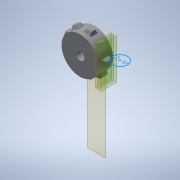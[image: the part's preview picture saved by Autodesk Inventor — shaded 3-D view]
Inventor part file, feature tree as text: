
AUTODESK INVENTOR PART (.ipt)
format: ipt  version: 2020 (Build 240168000, 168)  size: 642,048 bytes
history: native  units: mm
features: other x14, sketch x9, extrude x8, projected_geometry x2, loft x1, pattern_circular x1, chamfer x1, reference x1
ambient origin geometry x8: Origin, YZ Plane, XZ Plane, XY Plane, X Axis, Y Axis, Z Axis, Center Point
bodies: Body1 (feature_tree)
feature tree (37):
  other  "Bryła1"
  other  "Płaszczyzna konstrukcyjna1"
  extrude  "Wyciągnięcie proste1"  Depth=20.0mm
  other  "Płaszczyzna konstrukcyjna2"
  extrude  "Wyciągnięcie proste2"  Depth=50.0mm
  extrude  "Wyciągnięcie proste3"  Depth=20.0mm TaperAngle=0.0deg
  other  "Płaszczyzna konstrukcyjna4"
  other  "Płaszczyzna konstrukcyjna5"
  sketch  "Szkic5"
  other  "Płaszczyzna konstrukcyjna6"
  loft  "Wyciągnięcie złożone1"
  pattern_circular  "Szyk kołowy1"  [2 undecoded]
  extrude  "Wyciągnięcie proste5"  TaperAngle=0.0deg  [1 undecoded]
  other  "Zęby przekładni walcowej1"
  extrude  "Wyciągnięcie proste6"  Depth=3.0mm
  sketch  "Szkic10"
  extrude  "Wyciągnięcie proste9"  Depth=12.0mm
  extrude  "Wyciągnięcie proste8"  Depth=12.0mm
  extrude  "Wyciągnięcie proste10"  [1 undecoded]
  chamfer  "Faza2"  Distance=3.0mm
  sketch  "Szkic1"
  reference  "Odniesienie1"
  sketch  "Szkic3"
  sketch  "Szkic4"
  other  "Płaszczyzna konstrukcyjna3"
  sketch  "Szkic6"
  sketch  "Szkic8"
  other  "Przekładnia walcowa2"
  sketch  "Szkic9"
  projected_geometry  "Pętla rzutowana1"
  sketch  "Szkic12"
  projected_geometry  "Pętla rzutowana2"
  other  "<userpath>\Desktop\3d\scanning-robot\Assembly1.iam"
  other  "Assembly1.iam"
  other  "Tower Pro MG90S Micro servo:2"
  other  "Крышка корпуса:1"
  other  "base:1"
note: 4 required parameter values undecoded (feature->parameter linkage not recoverable at this tier; creation-order binding heuristic only, values carry confidence <= 0.55)
